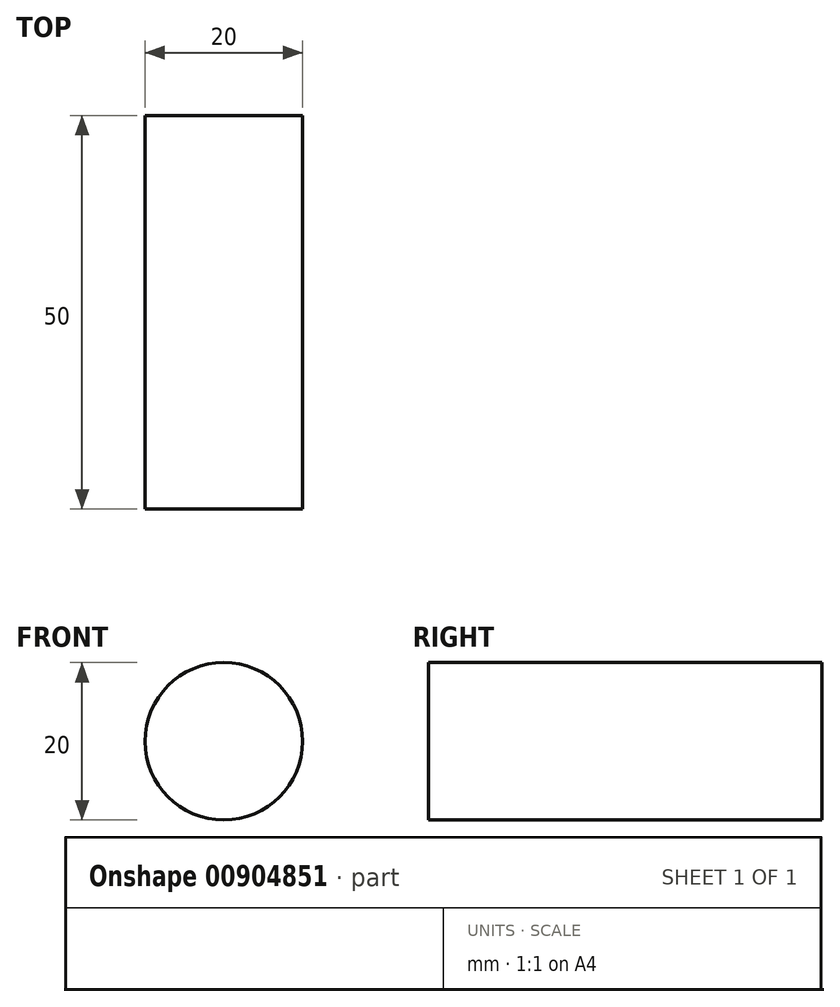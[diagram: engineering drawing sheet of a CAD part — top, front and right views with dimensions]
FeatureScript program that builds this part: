
annotation { "Feature Type Name" : "Feature", "Feature Type Description" : "" }
export const myFeature = defineFeature(function(context is Context, id is Id, definition is map)
    precondition{}
    {
        {
            var Q0;
            Q0=qCreatedBy(makeId("Front.planeOp"),FACE);
            var sketch = newSketch(context, id + "F0", { "sketchPlane" : qUnion([Q0])});
            skCircle(sketch, "E0", {"center": v(0, 0) * mm, "radius": 10 * mm});
            skSolve(sketch);
        }
        {
            var Q0;
            Q0 = qSketchRegion(id + "F0", true);
            extrude(context, id + "F1", {"entities" : qUnion([Q0]), "endBound" : BoundingType.SYMMETRIC, "depth" : 50 * mm, "offsetDistance" : 25 * mm});
        }
    });
